SOLIDWORKS PART (.sldprt)
format: sldprt  version: not decoded by parser v0  size: 423,424 bytes
history: native  units: mm
features: sketch x8, cut_extrude x6, extrude x2, plane x2, mirror x2, material x1, chamfer x1 (+13 scaffold rows collapsed)
feature tree (35):
  scaffold x13  (default folders/planes/origin — collapsed)
  material  "Material <not specified>"
  sketch  "Sketch2"  dims[D1=136.0mm D2=191.0mm]
  extrude  "Boss-Extrude1"  Depth=3mm
  plane  "Plane1"
  extrude  "Axis2"  [1 undecoded]
  plane  "Plane2"
  sketch  "Sketch3"  dims[c1.D6=~4.191383mm c1.D1=3.0mm c1.D2=10.0mm c1.D4=10.0mm c2.D6=20.0mm c2.D7=30.0mm c2.D8=21.0mm c2.D3=6.0 c2.D5=6.0]
  cut_extrude  "Cut-Extrude1"  [1 undecoded]
  mirror  "Mirror1"
  sketch  "Sketch4"  dims[D1=3.0mm D2=10.0mm D4=10.0mm D6=15.0mm D7=15.0mm D3=6.0 D5=5.0]
  cut_extrude  "Cut-Extrude2"  [1 undecoded]
  mirror  "Mirror2"
  sketch  "Sketch6"  dims[D1=106.0mm]
  sketch  "Sketch8"  dims[D1=10.0mm]
  cut_extrude  "Cut-Extrude3"  [1 undecoded]
  sketch  "Sketch9"  dims[D1=6.0mm]
  cut_extrude  "Cut-Extrude4"  [1 undecoded]
  sketch  "Sketch10"
  cut_extrude  "Cut-Extrude5"  [1 undecoded]
  sketch  "Sketch11"  dims[c1.D5=2.1mm c1.D6=2.1mm c1.D1=12.0mm c1.D2=10.0mm c2.D1=12.0mm c2.D2=10.0mm c2.D3=18.0mm c2.D4=15.0mm c2.D6=2.0mm c2.D7=10.0mm]
  cut_extrude  "Cut-Extrude6"  [1 undecoded]
  chamfer  "Chamfer1"  Distance=1mm Angle=45deg
decode coverage: 9 of 19 modeling features carry decoded parameters
note: ~ marks probable driven/reference dimensions
note: 7 parameter values undecoded
summary: no parameter record found for 7 features
note: suppression state not decoded; provenance and decode notes live in map.json
